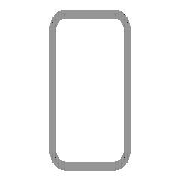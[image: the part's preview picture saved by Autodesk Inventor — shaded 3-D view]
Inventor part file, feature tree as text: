
AUTODESK INVENTOR PART (.ipt)
format: ipt  version: 2025 (Build 290162010, 162A)  size: 133,632 bytes
history: native  units: mm (DEFAULTED — no unit token found)
features: other x4, sketch x1, plane x1
ambient origin geometry x8: Origin, YZ Plane, XZ Plane, XY Plane, X Axis, Y Axis, Z Axis, Center Point
bodies: Solid1 (feature_tree), Body (feature_tree)
feature tree (6):
  parser-record x1  (decoder bookkeeping rows leaked as tree rows — omitted from the tree; the rows remain in map.json)
  other  "Driven Length"
  other  "Start Plane"
  other  "End Plane"
  sketch  "Sketch3"  dims[d3=760.0mm d4=0.0mm d7=6.0mm d9=40.0mm d11=60.0mm d12=3.0mm d13=20.0mm d14=780.0mm d15=20.0mm d16=30.0mm d17=90.0deg d18=760.0mm]
  plane  "Work Plane3"
